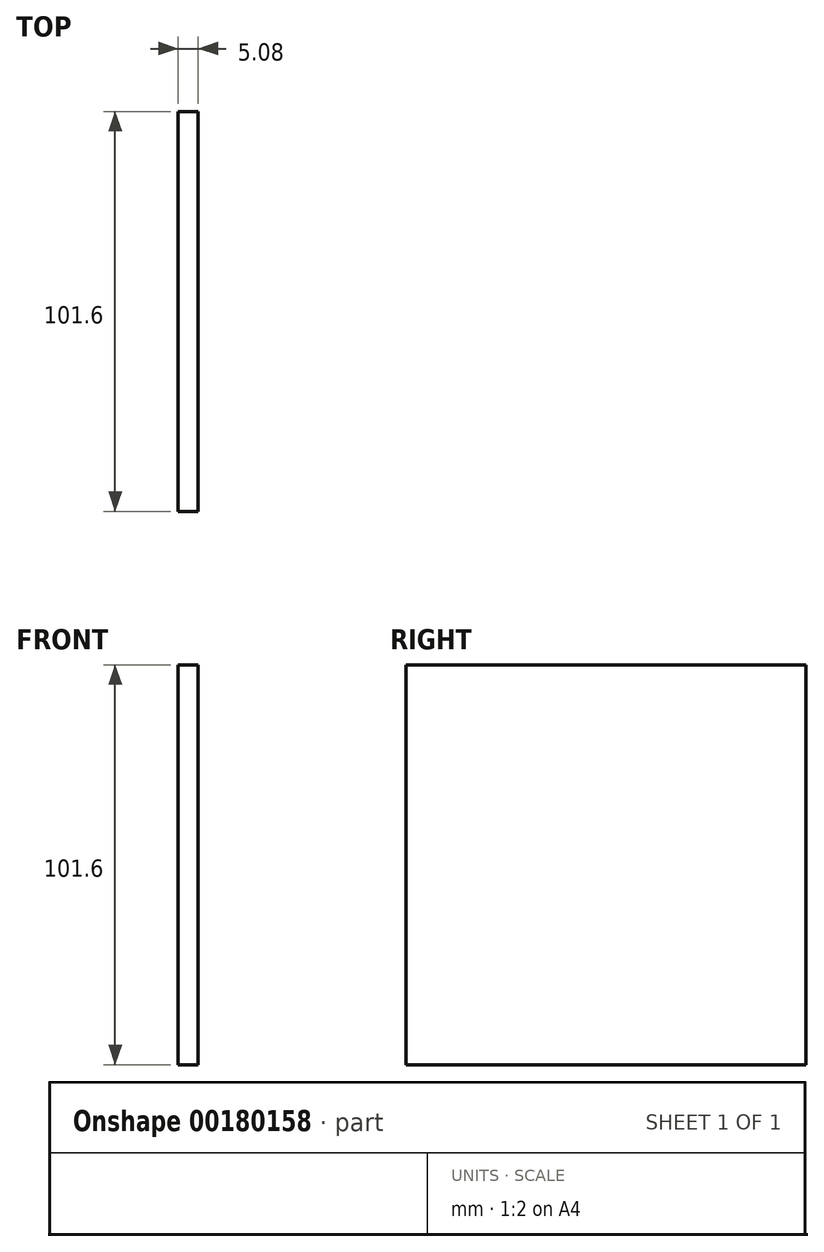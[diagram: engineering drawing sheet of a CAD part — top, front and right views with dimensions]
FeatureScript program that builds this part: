
annotation { "Feature Type Name" : "Feature", "Feature Type Description" : "" }
export const myFeature = defineFeature(function(context is Context, id is Id, definition is map)
    precondition{}
    {
        {
            var Q0;
            Q0=qCreatedBy(makeId("Right.planeOp"),FACE);
            var sketch = newSketch(context, id + "F0", { "sketchPlane" : qUnion([Q0])});
            skLineSegment(sketch, "E0.bottom", {"start": v(0, 0) * mm, "end": v(-101.6, 0) * mm});
            skLineSegment(sketch, "E0.top", {"start": v(0, 101.6) * mm, "end": v(-101.6, 101.6) * mm});
            skLineSegment(sketch, "E0.left", {"start": v(0, 0) * mm, "end": v(0, 101.6) * mm});
            skLineSegment(sketch, "E0.right", {"start": v(-101.6, 0) * mm, "end": v(-101.6, 101.6) * mm});
            skSolve(sketch);
        }
        {
            var Q0;
            Q0 = qSketchRegion(id + "F0", true);
            extrude(context, id + "F1", {"entities" : qUnion([Q0]), "depth" : 5.08 * mm});
        }
    });
